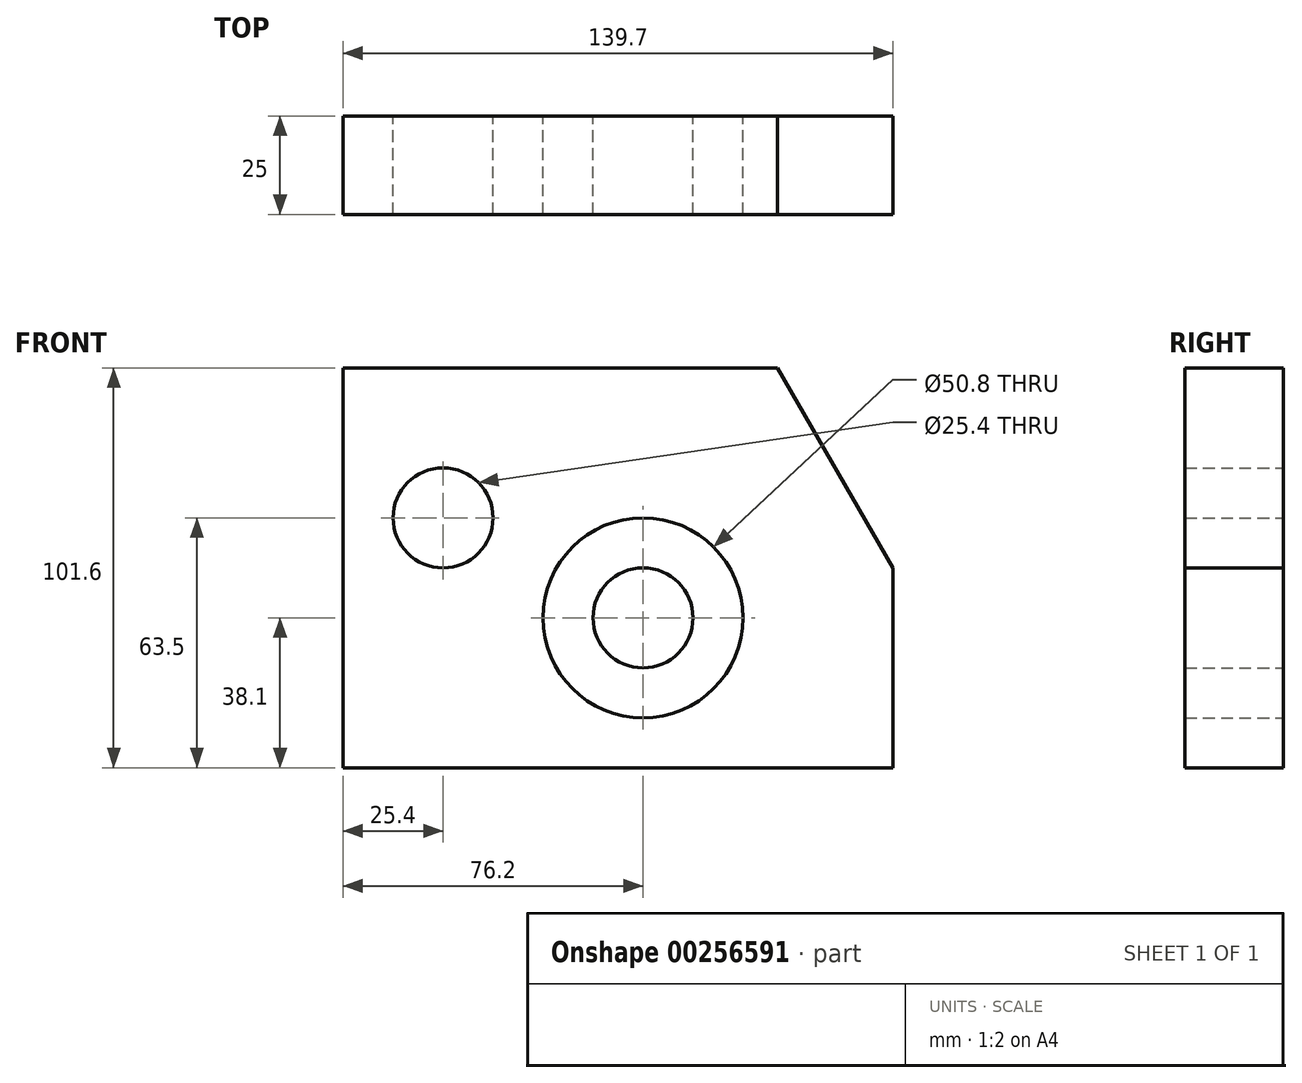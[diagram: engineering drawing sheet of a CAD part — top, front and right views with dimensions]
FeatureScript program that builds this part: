
annotation { "Feature Type Name" : "Feature", "Feature Type Description" : "" }
export const myFeature = defineFeature(function(context is Context, id is Id, definition is map)
    precondition{}
    {
        {
            var Q0;
            Q0=qCreatedBy(makeId("Front.planeOp"),FACE);
            var sketch = newSketch(context, id + "F0", { "sketchPlane" : qUnion([Q0])});
            skLineSegment(sketch, "E0.bottom", {"start": v(-76.2, 50.8) * mm, "end": v(34.17, 50.8) * mm});
            skLineSegment(sketch, "E0.top", {"start": v(-76.2, -50.8) * mm, "end": v(63.5, -50.8) * mm});
            skLineSegment(sketch, "E0.left", {"start": v(-76.2, 50.8) * mm, "end": v(-76.2, -50.8) * mm});
            skLineSegment(sketch, "E0.right", {"start": v(63.5, 0) * mm, "end": v(63.5, -50.8) * mm});
            skLineSegment(sketch, "E1", {"start": v(-76.2, -50.8) * mm, "end": v(-76.2, 12.7) * mm});
            skLineSegment(sketch, "E2", {"start": v(-76.2, 12.7) * mm, "end": v(-76.2, -50.8) * mm});
            skLineSegment(sketch, "E3", {"start": v(-76.2, -50.8) * mm, "end": v(0, -50.8) * mm});
            skLineSegment(sketch, "E4", {"start": v(-76.2, 50.8) * mm, "end": v(-50.8, 50.8) * mm});
            skLineSegment(sketch, "E5", {"start": v(63.5, -50.8) * mm, "end": v(63.5, 0) * mm});
            skLineSegment(sketch, "E6", {"start": v(63.5, 0) * mm, "end": v(48.3, 26.32) * mm});
            skLineSegment(sketch, "E7", {"start": v(63.5, 0) * mm, "end": v(34.17, 50.8) * mm});
            skCircle(sketch, "E8", {"center": v(0, -12.7) * mm, "radius": 12.7 * mm});
            skCircle(sketch, "E9", {"center": v(0, -12.7) * mm, "radius": 25.4 * mm});
            skCircle(sketch, "E10", {"center": v(-50.8, 12.7) * mm, "radius": 12.7 * mm});
            skPoint(sketch, "E11.trimOffspring.end.orphan", {"position": v(-50.8, 0) * mm});
            skSolve(sketch);
        }
        {
            var Q0;
            {var subQ0=sQuery(id+"F0.wireOp",EDGE,"E0.bottom");Q0=makeQuery(id+"F0.imprint","IMPRINT",FACE,{"disambiguationData":[TD([[makeQuery(id+"F0.imprint","IMPRINT",EDGE,{"derivedFrom":subQ0}),-1.0]])]});}
            var Q1;
            Q1=makeQuery(id+"F0.imprint","IMPRINT",FACE,{"disambiguationData":[TD([[makeQuery(id+"F0.imprint","IMPRINT",EDGE,{"derivedFrom":sQuery(id+"F0.wireOp",EDGE,"E8")}),1.0]])]});
            extrude(context, id + "F1", {"entities" : qUnion([Q0, Q1]), "depth" : 25 * mm});
        }
    });
